# Revit family: MSR-Schutz für 2-polige Stromversorgung12V-24V-48V-60V-110V-230V
name_source: partatom
category: Generic Models
revit_build: Autodesk Revit 2015 (Build: 20140606_1530(x64)
units: mm (PartAtom-declared; Revit-internal decimal feet)

## types (6) — shared parameters
Cut depth = 12 mm  [stored 0.0393701 ft]
Height = 61 mm
Length = 18 mm
Manufacturer = OBO Bettermann
Material = OBO PA 6 GF20
Material 2 = OBO PE
URL = http://www.obo-bettermann.com
Width = 90 mm  [stored 0.295276 ft]

## per-type parameters (varying)
| type | GTIN | Manufacturer Art.No. |
| VF12-AC DC | 4012195578116 | 5097453 |
| VF24-AC/DC | 4012195578123 | 5097607 |
| VF48-AC/DC | 4012195578130 | 5097615 |
| VF60-AC/DC | 4012195578147 | 5097623 |
| VF110-AC DC | 4012195578154 | 5097631 |
| VF230-AC/DC | 4012195578161 | 5097650 |

note: column(s) folded — value = type name in every type: Article Type

note: [stored X ft] marks values corroborated as IEEE doubles in the binary element streams (Revit-internal decimal feet)

## geometry (parser evidence)
native form markers: Sweep x1
no freeform markers — native parametric forms only
